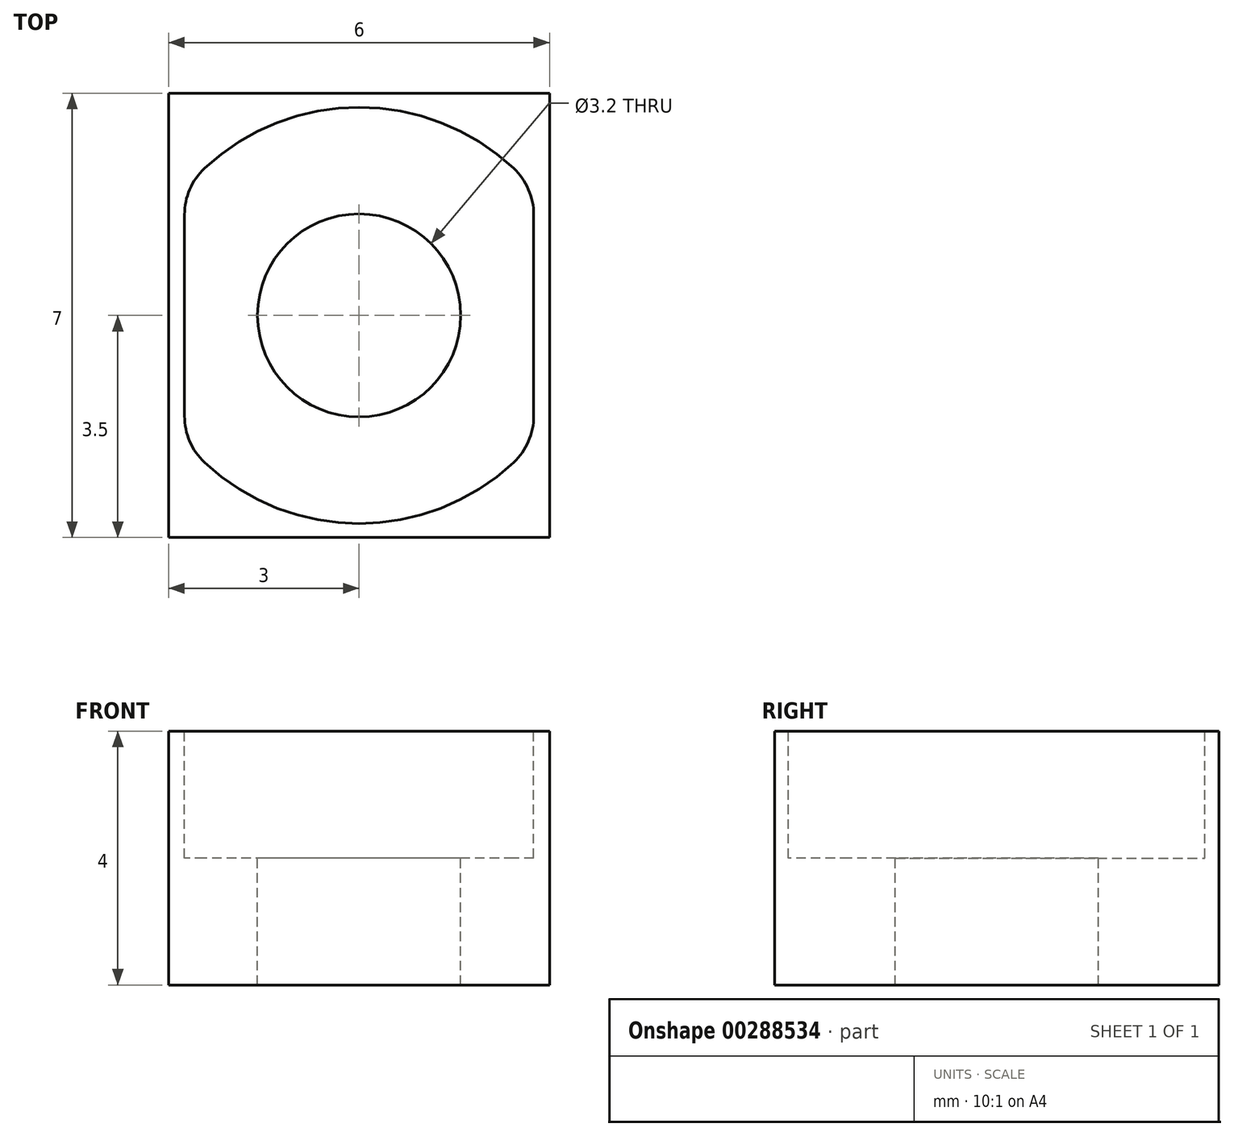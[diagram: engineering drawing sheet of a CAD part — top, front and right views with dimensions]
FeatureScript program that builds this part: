
annotation { "Feature Type Name" : "Feature", "Feature Type Description" : "" }
export const myFeature = defineFeature(function(context is Context, id is Id, definition is map)
    precondition{}
    {
        {
            var Q0;
            Q0=qCreatedBy(makeId("Top.planeOp"),FACE);
            var sketch = newSketch(context, id + "F0", { "sketchPlane" : qUnion([Q0])});
            skLineSegment(sketch, "E0.bottom", {"start": v(3, -3.5) * mm, "end": v(-3, -3.5) * mm});
            skLineSegment(sketch, "E0.top", {"start": v(3, 3.5) * mm, "end": v(-3, 3.5) * mm});
            skLineSegment(sketch, "E0.left", {"start": v(3, -3.5) * mm, "end": v(3, 3.5) * mm});
            skLineSegment(sketch, "E0.right", {"start": v(-3, -3.5) * mm, "end": v(-3, 3.5) * mm});
            skPoint(sketch, "E0.middle", {"position": v(0, 0) * mm});
            skCircle(sketch, "E1", {"center": v(0, 0) * mm, "radius": 1.6 * mm});
            skCircle(sketch, "E2.cCircle", {"center": v(0, 0) * mm, "radius": 2.75 * mm, "construction": true});
            skLineSegment(sketch, "E2.0", {"start": v(2.75, 1.59) * mm, "end": v(2.75, -1.59) * mm});
            skLineSegment(sketch, "E2.1", {"start": v(2.75, -1.59) * mm, "end": v(0, -3.18) * mm, "construction": true});
            skLineSegment(sketch, "E2.2", {"start": v(0, -3.18) * mm, "end": v(-2.75, -1.59) * mm, "construction": true});
            skLineSegment(sketch, "E2.3", {"start": v(-2.75, -1.59) * mm, "end": v(-2.75, 1.59) * mm});
            skLineSegment(sketch, "E2.4", {"start": v(-2.75, 1.59) * mm, "end": v(0, 3.18) * mm, "construction": true});
            skLineSegment(sketch, "E2.5", {"start": v(0, 3.18) * mm, "end": v(2.75, 1.59) * mm, "construction": true});
            skPoint(sketch, "E2.0.midPoint", {"position": v(2.75, 0) * mm});
            skArc(sketch, "E3", {"start": v(-2.75, 1.59) * mm, "mid": v(-2.67, 1.99) * mm, "end": v(-2.43, 2.32) * mm});
            skArc(sketch, "E4", {"start": v(2.75, 1.59) * mm, "mid": v(2.67, 1.99) * mm, "end": v(2.43, 2.32) * mm});
            skLineSegment(sketch, "E5", {"start": v(-2.43, 2.32) * mm, "end": v(-1.75, 1.59) * mm, "construction": true});
            skLineSegment(sketch, "E6", {"start": v(1.75, 1.59) * mm, "end": v(2.43, 2.32) * mm, "construction": true});
            skLineSegment(sketch, "E7", {"start": v(-2.43, 2.32) * mm, "end": v(0, 4.6) * mm, "construction": true});
            skLineSegment(sketch, "E8", {"start": v(2.43, 2.32) * mm, "end": v(0, 4.6) * mm, "construction": true});
            skArc(sketch, "E9", {"start": v(-2.75, -1.59) * mm, "mid": v(-2.67, -1.99) * mm, "end": v(-2.43, -2.32) * mm});
            skArc(sketch, "E10", {"start": v(2.75, -1.59) * mm, "mid": v(2.67, -1.99) * mm, "end": v(2.43, -2.32) * mm});
            skLineSegment(sketch, "E11", {"start": v(-1.75, -1.59) * mm, "end": v(-2.43, -2.32) * mm, "construction": true});
            skLineSegment(sketch, "E12", {"start": v(-2.43, -2.32) * mm, "end": v(0, -4.6) * mm, "construction": true});
            skLineSegment(sketch, "E13", {"start": v(1.75, -1.59) * mm, "end": v(2.43, -2.32) * mm, "construction": true});
            skLineSegment(sketch, "E14", {"start": v(2.43, -2.32) * mm, "end": v(0, -4.6) * mm, "construction": true});
            skArc(sketch, "E15", {"start": v(-2.43, 2.32) * mm, "mid": v(0, 3.28) * mm, "end": v(2.43, 2.32) * mm});
            skArc(sketch, "E16", {"start": v(-2.43, -2.32) * mm, "mid": v(0, -3.28) * mm, "end": v(2.43, -2.32) * mm});
            skSolve(sketch);
        }
        {
            var Q0;
            Q0=makeQuery(id+"F0.imprint","IMPRINT",FACE,{"disambiguationData":[TD([[makeQuery(id+"F0.imprint","IMPRINT",EDGE,{"derivedFrom":sQuery(id+"F0.wireOp",EDGE,"E0.bottom")}),-1.0]])]});
            var Q1;
            {var subQ1=sQuery(id+"F0.wireOp",EDGE,"E2.4");var subQ3=sQuery(id+"F0.wireOp",EDGE,"E5");var subQ4=makeQuery(id+"F0.imprint","INTERSECT",VERTEX,{"derivedFrom":[subQ1,subQ3]});Q1=makeQuery(id+"F0.imprint","IMPRINT",FACE,{"disambiguationData":[TD([[makeQuery(id+"F0.imprint","IMPRINT",EDGE,{"disambiguationData":[TD([[subQ4,-1.0]])],"derivedFrom":subQ1}),1.0]])]});}
            var Q2;
            {var subQ0=sQuery(id+"F0.wireOp",EDGE,"E3");Q2=makeQuery(id+"F0.imprint","IMPRINT",FACE,{"disambiguationData":[TD([[makeQuery(id+"F0.imprint","IMPRINT",EDGE,{"derivedFrom":subQ0}),-1.0]])]});}
            var Q3;
            {var subQ1=sQuery(id+"F0.wireOp",EDGE,"E2.5");var subQ3=sQuery(id+"F0.wireOp",EDGE,"E6");var subQ4=makeQuery(id+"F0.imprint","INTERSECT",VERTEX,{"derivedFrom":[subQ1,subQ3]});Q3=makeQuery(id+"F0.imprint","IMPRINT",FACE,{"disambiguationData":[TD([[makeQuery(id+"F0.imprint","IMPRINT",EDGE,{"disambiguationData":[TD([[subQ4,1.0]])],"derivedFrom":subQ1}),1.0]])]});}
            var Q4;
            {var subQ0=sQuery(id+"F0.wireOp",EDGE,"E4");Q4=makeQuery(id+"F0.imprint","IMPRINT",FACE,{"disambiguationData":[TD([[makeQuery(id+"F0.imprint","IMPRINT",EDGE,{"derivedFrom":subQ0}),1.0]])]});}
            var Q5;
            Q5=makeQuery(id+"F0.imprint","IMPRINT",FACE,{"disambiguationData":[TD([[makeQuery(id+"F0.imprint","IMPRINT",EDGE,{"derivedFrom":sQuery(id+"F0.wireOp",EDGE,"E1")}),-1.0]])]});
            var Q6;
            {var subQ1=sQuery(id+"F0.wireOp",EDGE,"E2.1");var subQ3=sQuery(id+"F0.wireOp",EDGE,"E13");var subQ4=makeQuery(id+"F0.imprint","INTERSECT",VERTEX,{"derivedFrom":[subQ1,subQ3]});Q6=makeQuery(id+"F0.imprint","IMPRINT",FACE,{"disambiguationData":[TD([[makeQuery(id+"F0.imprint","IMPRINT",EDGE,{"disambiguationData":[TD([[subQ4,-1.0]])],"derivedFrom":subQ1}),1.0]])]});}
            var Q7;
            {var subQ0=sQuery(id+"F0.wireOp",EDGE,"E10");Q7=makeQuery(id+"F0.imprint","IMPRINT",FACE,{"disambiguationData":[TD([[makeQuery(id+"F0.imprint","IMPRINT",EDGE,{"derivedFrom":subQ0}),-1.0]])]});}
            var Q8;
            {var subQ1=sQuery(id+"F0.wireOp",EDGE,"E2.2");var subQ3=sQuery(id+"F0.wireOp",EDGE,"E11");var subQ4=makeQuery(id+"F0.imprint","INTERSECT",VERTEX,{"derivedFrom":[subQ1,subQ3]});Q8=makeQuery(id+"F0.imprint","IMPRINT",FACE,{"disambiguationData":[TD([[makeQuery(id+"F0.imprint","IMPRINT",EDGE,{"disambiguationData":[TD([[subQ4,1.0]])],"derivedFrom":subQ1}),1.0]])]});}
            var Q9;
            {var subQ0=sQuery(id+"F0.wireOp",EDGE,"E9");Q9=makeQuery(id+"F0.imprint","IMPRINT",FACE,{"disambiguationData":[TD([[makeQuery(id+"F0.imprint","IMPRINT",EDGE,{"derivedFrom":subQ0}),1.0]])]});}
            extrude(context, id + "F1", {"entities" : qUnion([Q0, Q1, Q2, Q3, Q4, Q5, Q6, Q7, Q8, Q9]), "oppositeDirection" : true, "depth" : 4 * mm});
        }
        {
            var Q0;
            Q0=makeQuery(id+"F0.imprint","IMPRINT",FACE,{"disambiguationData":[TD([[makeQuery(id+"F0.imprint","IMPRINT",EDGE,{"derivedFrom":sQuery(id+"F0.wireOp",EDGE,"E1")}),-1.0]])]});
            var Q1;
            Q1=makeQuery(id+"F0.imprint","IMPRINT",FACE,{"disambiguationData":[TD([[makeQuery(id+"F0.imprint","IMPRINT",EDGE,{"derivedFrom":sQuery(id+"F0.wireOp",EDGE,"E2.4")}),1.0]])]});
            var Q2;
            Q2=makeQuery(id+"F0.imprint","IMPRINT",FACE,{"disambiguationData":[TD([[makeQuery(id+"F0.imprint","IMPRINT",EDGE,{"derivedFrom":sQuery(id+"F0.wireOp",EDGE,"E2.1")}),1.0]])]});
            var Q3;
            {var subQ1=sQuery(id+"F0.wireOp",EDGE,"E2.5");var subQ3=sQuery(id+"F0.wireOp",EDGE,"E6");var subQ4=makeQuery(id+"F0.imprint","INTERSECT",VERTEX,{"derivedFrom":[subQ1,subQ3]});Q3=makeQuery(id+"F0.imprint","IMPRINT",FACE,{"disambiguationData":[TD([[makeQuery(id+"F0.imprint","IMPRINT",EDGE,{"disambiguationData":[TD([[subQ4,1.0]])],"derivedFrom":subQ1}),1.0]])]});}
            var Q4;
            {var subQ0=sQuery(id+"F0.wireOp",EDGE,"E4");Q4=makeQuery(id+"F0.imprint","IMPRINT",FACE,{"disambiguationData":[TD([[makeQuery(id+"F0.imprint","IMPRINT",EDGE,{"derivedFrom":subQ0}),1.0]])]});}
            var Q5;
            {var subQ1=sQuery(id+"F0.wireOp",EDGE,"E2.2");var subQ3=sQuery(id+"F0.wireOp",EDGE,"E11");var subQ4=makeQuery(id+"F0.imprint","INTERSECT",VERTEX,{"derivedFrom":[subQ1,subQ3]});Q5=makeQuery(id+"F0.imprint","IMPRINT",FACE,{"disambiguationData":[TD([[makeQuery(id+"F0.imprint","IMPRINT",EDGE,{"disambiguationData":[TD([[subQ4,1.0]])],"derivedFrom":subQ1}),1.0]])]});}
            var Q6;
            {var subQ0=sQuery(id+"F0.wireOp",EDGE,"E9");Q6=makeQuery(id+"F0.imprint","IMPRINT",FACE,{"disambiguationData":[TD([[makeQuery(id+"F0.imprint","IMPRINT",EDGE,{"derivedFrom":subQ0}),1.0]])]});}
            extrude(context, id + "F2", {"entities" : qUnion([Q0, Q1, Q2, Q3, Q4, Q5, Q6]), "operationType" : NewBodyOperationType.REMOVE, "oppositeDirection" : true, "depth" : 2 * mm});
        }
    });
